# Revit family: Sanitary_Showers_hansgrohe_26720XXX-Raindance-Select-E-Shower-holde__
name_source: partatom
category: Plumbing Fixtures
revit_build: Autodesk Revit 2018 (Build: 20170223_1515(x64)
units: mm (PartAtom-declared; Revit-internal decimal feet)

## family parameters
Always vertical = No
Cut with Voids When Loaded = No
OmniClass Number = 23.45.05.14.17
OmniClass Title = Showers
Part Type = Normal
Room Calculation Point = No
Round Connector Dimension = Use Diameter
Shared = No
Work Plane-Based = Yes

## types (2) — shared parameters
BIMobject category = Showers
Default Elevation = 1219.2 mm  [stored 4 ft]
Description = Raindance Select E Shower holder set 120 3jet with shower hose 160 cm
Edition number = 1
IFC Classification = Sanitary Terminal
Manufacturer = Hansgrohe
Manufacturer name = hansgrohe
Masterformat 2014 Code = 22 41 23
Masterformat 2014 Description = Residential Showers
Material 2 = Hansgrohe - Metal - 000 Chrome
Model = 26720XXX
NBS Reference Code = 35-06-81
NBS Reference Description = Shower Heads
OmniClass Code = 23-31 17 19
OmniClass Description = Shower Head Fixtures
Product Guid = 6a2481ae-490a-4e6a-8f2b-bda08ccf5aa3
Product SKU = 26720XXX
Product data url = https://bimobject.com
Product family = Raindance Select E
Product group = Hand showers
Product name = 26720XXX Raindance Select E Shower holder set 120 3jet with shower hose 160 cm
QR code = https://www.bimobject.com
UNSPSC Code = 30181503
URL = https://www.hansgrohe.com
Uniclass 2015 Code = Pr_40_20_87_76
Uniclass 2015 Name = Shower heads
Uniformat II Code = D2010
Uniformat II Description = Plumbing Fixtures

## per-type parameters (varying)
| type | Material 1 |
| 000 Chrome | Hansgrohe - Metal - 000 Chrome |
| 400 White/Chrome | Hansgrohe - Plastic - White |

note: [stored X ft] marks values corroborated as IEEE doubles in the binary element streams (Revit-internal decimal feet)

## geometry (parser evidence)
native form markers: Sweep x1
no freeform markers — native parametric forms only
